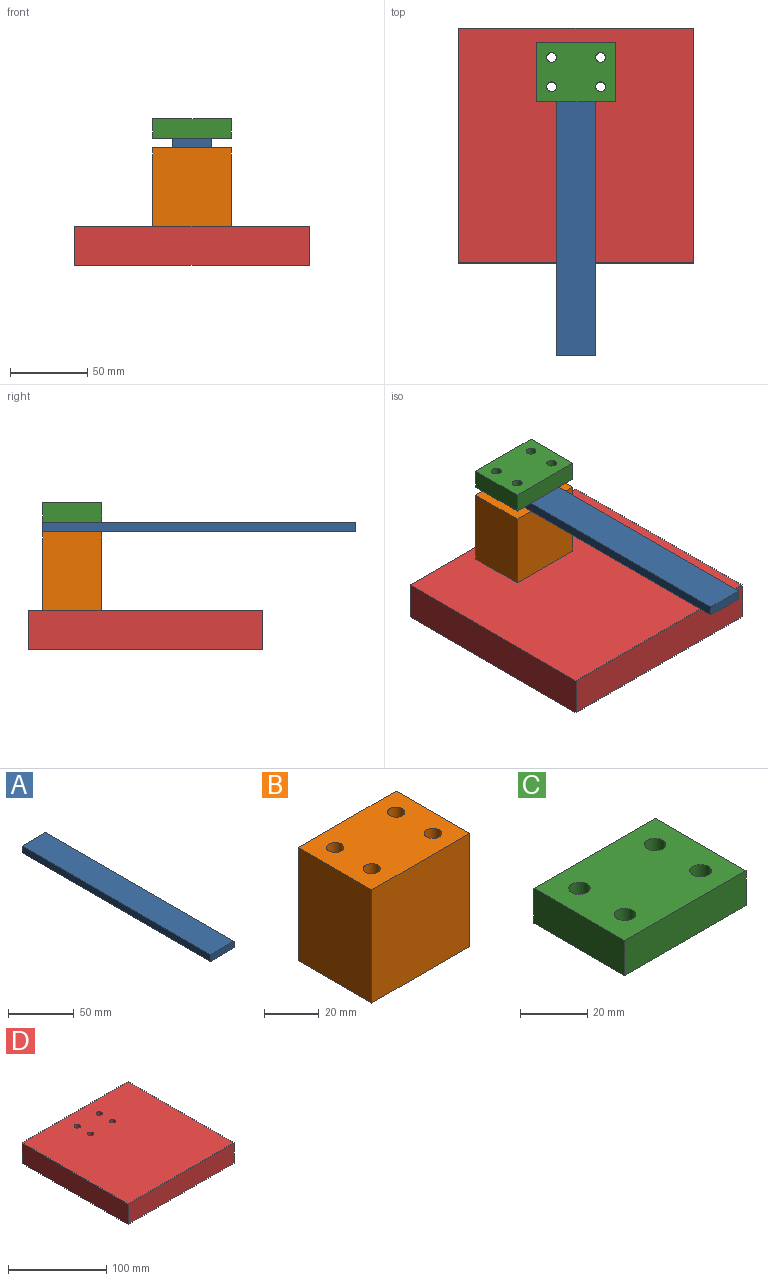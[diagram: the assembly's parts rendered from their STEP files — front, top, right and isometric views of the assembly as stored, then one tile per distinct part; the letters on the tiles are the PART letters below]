
ASSEMBLY  parts=4 mates=3
PART A: 6 faces, bbox 25.4x203.2x6.4 mm
  f0: plane 25.4x6.35mm, normal (0,1,0), area 161.3mm2, adj f1,f3,f4,f5
  f1: plane 203.2x6.35mm, normal (-1,0,0), area 1290.3mm2, adj f0,f2,f4,f5
  f2: plane 25.4x6.35mm, normal (0,-1,0), area 161.3mm2, adj f1,f3,f4,f5
  f3: plane 203.2x6.35mm, normal (1,0,0), area 1290.3mm2, adj f0,f2,f4,f5
  f4: plane 203.2x25.4mm, normal (0,0,1), area 5161.3mm2, adj f0,f1,f2,f3
  f5: plane 203.2x25.4mm, normal (0,0,-1), area 5161.3mm2, adj f0,f1,f2,f3
PART B: 10 faces, bbox 50.8x38.1x50.8 mm
  f0: plane 50.8x38.1mm, normal (0,0,1), area 1808.8mm2, adj f1,f3,f4,f5,f6,f7,f8,f9
  f1: plane 50.8x38.1mm, normal (-1,0,0), area 1935.5mm2, adj f0,f2,f4,f5
  f2: plane 50.8x38.1mm, normal (0,0,-1), area 1808.8mm2, adj f1,f3,f4,f5,f6,f7,f8,f9
  f3: plane 50.8x38.1mm, normal (1,0,0), area 1935.5mm2, adj f0,f2,f4,f5
  f4: plane 50.8x50.8mm, normal (0,-1,0), area 2580.6mm2, adj f0,f1,f2,f3
  f5: plane 50.8x50.8mm, normal (0,1,0), area 2580.6mm2, adj f0,f1,f2,f3
  f6: cylinder r=3.17mm len=50.8mm, axis (0,0,-1), area 1013.4mm2, adj f0,f2
  f7: cylinder r=3.17mm len=50.8mm, axis (0,0,-1), area 1013.4mm2, adj f0,f2
  f8: cylinder r=3.17mm len=50.8mm, axis (0,0,-1), area 1013.4mm2, adj f0,f2
  f9: cylinder r=3.18mm len=50.8mm, axis (0,0,-1), area 1013.4mm2, adj f0,f2
PART C: 10 faces, bbox 50.8x38.1x12.7 mm
  f0: plane 50.8x38.1mm, normal (0,0,1), area 1808.8mm2, adj f1,f3,f4,f5,f6,f7,f8,f9
  f1: plane 38.1x12.7mm, normal (-1,0,0), area 483.9mm2, adj f0,f2,f4,f5
  f2: plane 50.8x38.1mm, normal (0,0,-1), area 1808.8mm2, adj f1,f3,f4,f5,f6,f7,f8,f9
  f3: plane 38.1x12.7mm, normal (1,0,0), area 483.9mm2, adj f0,f2,f4,f5
  f4: plane 50.8x12.7mm, normal (0,-1,0), area 645.2mm2, adj f0,f1,f2,f3
  f5: plane 50.8x12.7mm, normal (0,1,0), area 645.2mm2, adj f0,f1,f2,f3
  f6: cylinder r=3.17mm len=12.7mm, axis (0,0,-1), area 253.4mm2, adj f0,f2
  f7: cylinder r=3.17mm len=12.7mm, axis (0,0,-1), area 253.4mm2, adj f0,f2
  f8: cylinder r=3.17mm len=12.7mm, axis (0,0,-1), area 253.4mm2, adj f0,f2
  f9: cylinder r=3.18mm len=12.7mm, axis (0,0,-1), area 253.4mm2, adj f0,f2
PART D: 18 faces, bbox 152.4x152.4x25.4 mm
  f0: plane 152.4x25.4mm, normal (0,1,0), area 3871mm2, adj f1,f3,f4,f5
  f1: plane 152.4x25.4mm, normal (-1,0,0), area 3871mm2, adj f0,f2,f4,f5
  f2: plane 152.4x25.4mm, normal (0,-1,0), area 3871mm2, adj f1,f3,f4,f5
  f3: plane 152.4x25.4mm, normal (1,0,0), area 3871mm2, adj f0,f2,f4,f5
  f4: plane 152.4x152.4mm, normal (0,0,1), area 23099.1mm2, adj f0,f1,f2,f3,f6,f7,f8,f9
  f5: plane 152.4x152.4mm, normal (0,0,-1), area 22719.1mm2, adj f0,f1,f2,f3,f10,f12,f14,f16
  f6: cylinder r=3.17mm len=12.7mm, axis (0,0,-1), area 253.4mm2, adj f4,f17
  f7: cylinder r=3.17mm len=12.7mm, axis (0,0,-1), area 253.4mm2, adj f4,f15
  f8: cylinder r=3.17mm len=12.7mm, axis (0,0,-1), area 253.4mm2, adj f4,f13
  f9: cylinder r=3.17mm len=12.7mm, axis (0,0,-1), area 253.4mm2, adj f4,f11
  f10: cylinder r=6.35mm len=12.7mm, axis (0,0,-1), area 506.7mm2, adj f5,f11
  f11: plane 12.7x12.7mm, normal (0,0,-1), area 95mm2, adj f9,f10
  f12: cylinder r=6.35mm len=12.7mm, axis (0,0,-1), area 506.7mm2, adj f5,f13
  f13: plane 12.7x12.7mm, normal (0,0,-1), area 95mm2, adj f8,f12
  f14: cylinder r=6.35mm len=12.7mm, axis (0,0,-1), area 506.7mm2, adj f5,f15
  f15: plane 12.7x12.7mm, normal (0,0,-1), area 95mm2, adj f7,f14
  f16: cylinder r=6.35mm len=12.7mm, axis (0,0,-1), area 506.7mm2, adj f5,f17
  f17: plane 12.7x12.7mm, normal (0,0,-1), area 95mm2, adj f6,f16
PLACE A t=(-120.1,49.91,-59.79)mm
PLACE B t=(-144.35,126.4,-56.47)mm
PLACE C t=(-144.35,126.4,-62.82)mm
PLACE D t=(-126.26,130.4,-135.99)mm
MATE fastened B.f0 <-> A.f5  axis (0,0,1) through (-131.95,126.4,-59.79)mm
MATE fastened A.f4 <-> C.f2  axis (0,0,1) through (-131.95,126.4,-53.44)mm
MATE fastened B.f8 <-> D.f9  axis (0,0,-1) through (-116.08,116.87,-110.59)mm
